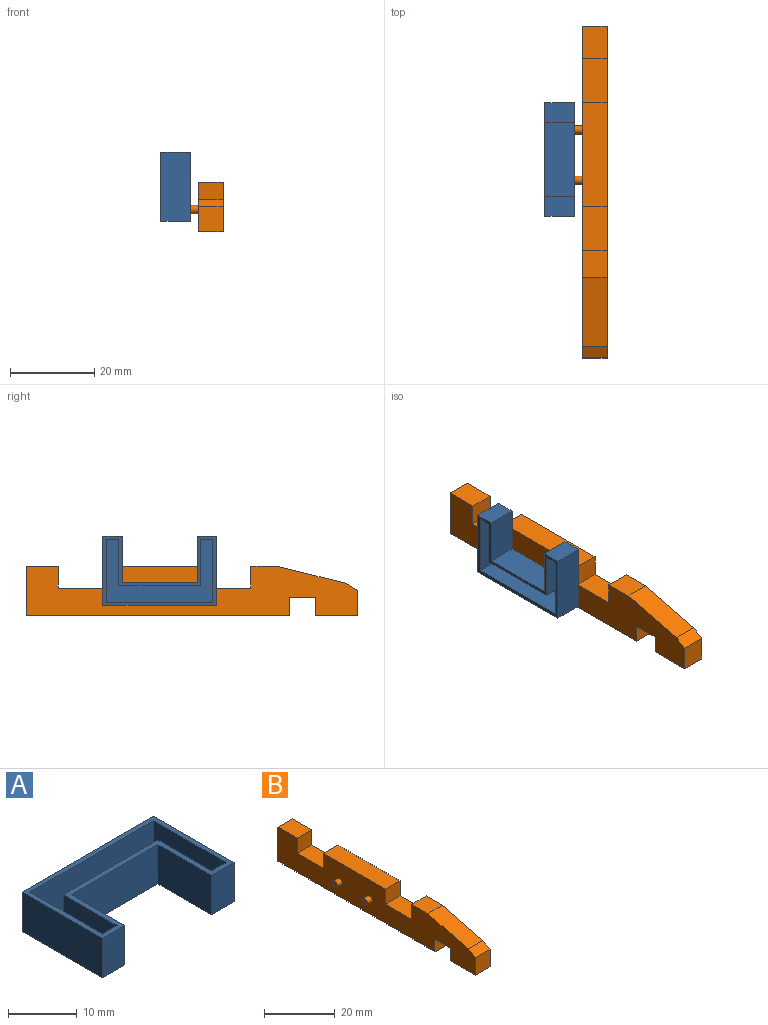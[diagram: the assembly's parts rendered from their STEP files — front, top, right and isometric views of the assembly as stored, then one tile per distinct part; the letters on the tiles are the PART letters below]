
ASSEMBLY  parts=2 mates=2
PART A: 19 faces, bbox 27x16.5x7 mm
  f0: plane 14.9x6.2mm, normal (1,0,0), area 92.4mm2, adj f1,f15,f16,f18
  f1: plane 25.4x6.2mm, normal (0,-1,0), area 157.5mm2, adj f0,f2,f16,f18
  f2: plane 14.9x6.2mm, normal (-1,0,0), area 92.4mm2, adj f1,f3,f16,f18
  f3: plane 6.2x3mm, normal (0,1,0), area 18.6mm2, adj f2,f4,f16,f18
  f4: plane 11x6.2mm, normal (1,0,0), area 68.2mm2, adj f3,f5,f16,f18
  f5: plane 19.4x6.2mm, normal (0,1,0), area 120.3mm2, adj f4,f6,f16,f18
  f6: plane 11x6.2mm, normal (-1,0,0), area 68.2mm2, adj f5,f15,f16,f18
  f7: plane 16.5x7mm, normal (-1,0,0), area 115.5mm2, adj f8,f14,f16,f17
  f8: plane 7x4.6mm, normal (0,-1,0), area 32.2mm2, adj f7,f9,f16,f17
  f9: plane 11x7mm, normal (1,0,0), area 77mm2, adj f8,f10,f16,f17
  f10: plane 17.8x7mm, normal (0,-1,0), area 124.6mm2, adj f9,f11,f16,f17
  f11: plane 11x7mm, normal (-1,0,0), area 77mm2, adj f10,f12,f16,f17
  f12: plane 7x4.6mm, normal (0,-1,0), area 32.2mm2, adj f11,f13,f16,f17
  f13: plane 16.5x7mm, normal (1,0,0), area 115.5mm2, adj f12,f14,f16,f17
  f14: plane 27x7mm, normal (0,1,0), area 189mm2, adj f7,f13,f16,f17
  f15: plane 6.2x3mm, normal (0,1,0), area 18.6mm2, adj f0,f6,f16,f18
  f16: plane 27x16.5mm, normal (0,0,1), area 84.6mm2, adj f0,f1,f2,f3,f4,f5,f6,f7
  f17: plane 27x16.5mm, normal (0,0,-1), area 249.7mm2, adj f7,f8,f9,f10,f11,f12,f13,f14
  f18: plane 25.4x14.9mm, normal (0,0,1), area 165.1mm2, adj f0,f1,f2,f3,f4,f5,f6,f15
PART B: 42 faces, bbox 7.8x79x11.8 mm
  f0: plane 5.1x5mm, normal (0,1,0), area 25.5mm2, adj f1,f17,f35,f37
  f1: plane 7.8x5mm, normal (0,0,1), area 39mm2, adj f0,f2,f35,f37
  f2: plane 5x4.3mm, normal (0,-1,0), area 21.5mm2, adj f1,f3,f35,f37
  f3: plane 8.4x5mm, normal (0,0,1), area 42mm2, adj f2,f4,f35,f37
  f4: plane 5x4.75mm, normal (0,1,0), area 23.7mm2, adj f3,f5,f35,f37
  f5: plane 5x2.31mm, normal (0,0.52,-0.85), area 13.5mm2, adj f4,f6,f35,f37
  f6: plane 16.09x5mm, normal (0,0.24,-0.97), area 82.9mm2, adj f5,f7,f35,f37
  f7: plane 5.5x5mm, normal (0,0,-1), area 27.5mm2, adj f6,f8,f35,f37
  f8: plane 5.2x5mm, normal (0,-1,0), area 26mm2, adj f7,f9,f35,f37
  f9: plane 12.1x5mm, normal (0,0,-1), area 60.5mm2, adj f8,f10,f35,f37
  f10: plane 5.2x5mm, normal (0,1,0), area 26mm2, adj f9,f11,f35,f37
  f11: plane 23.2x5mm, normal (0,0,-1), area 116mm2, adj f10,f12,f35,f37
  f12: plane 5.2x5mm, normal (0,-1,0), area 26mm2, adj f11,f13,f35,f37
  f13: plane 12.1x5mm, normal (0,0,-1), area 60.5mm2, adj f12,f14,f35,f37
  f14: plane 5.2x5mm, normal (0,1,0), area 26mm2, adj f13,f15,f35,f37
  f15: plane 6.1x5mm, normal (0,0,-1), area 30.5mm2, adj f14,f16,f35,f37
  f16: plane 11x5mm, normal (0,-1,0), area 55mm2, adj f15,f17,f35,f37
  f17: plane 62.8x5.8mm, normal (0,0,-1), area 58.2mm2, adj f0,f16,f18,f34,f35,f36,f37
  f18: plane 11.8x5.8mm, normal (0,1,0), area 68.4mm2, adj f17,f19,f35,f36
  f19: plane 7.7x5.8mm, normal (0,0,1), area 44.7mm2, adj f18,f20,f35,f36
  f20: plane 5.8x5.2mm, normal (0,-1,0), area 30.2mm2, adj f19,f21,f35,f36
  f21: plane 10.5x5.8mm, normal (0,0,1), area 60.9mm2, adj f20,f22,f35,f36
  f22: plane 5.8x5.2mm, normal (0,1,0), area 30.2mm2, adj f21,f23,f35,f36
  f23: plane 24.8x5.8mm, normal (0,0,1), area 143.8mm2, adj f22,f24,f35,f36
  f24: plane 5.8x5.2mm, normal (0,-1,0), area 30.2mm2, adj f23,f25,f35,f36
  f25: plane 10.5x5.8mm, normal (0,0,1), area 60.9mm2, adj f24,f26,f35,f36
  f26: plane 5.8x5.2mm, normal (0,1,0), area 30.2mm2, adj f25,f27,f35,f36
  f27: plane 6.4x5.8mm, normal (0,0,1), area 37.1mm2, adj f26,f28,f35,f36
  f28: plane 16.3x5.8mm, normal (0,-0.24,0.97), area 97.5mm2, adj f27,f29,f35,f36
  f29: plane 5.8x2.8mm, normal (0,-0.52,0.85), area 19mm2, adj f28,f30,f35,f36
  f30: plane 6x5.8mm, normal (0,-1,0), area 34.8mm2, adj f29,f31,f35,f36
  f31: plane 10x5.8mm, normal (0,0,-1), area 58mm2, adj f30,f32,f35,f36
  f32: plane 5.8x4.3mm, normal (0,1,0), area 24.9mm2, adj f31,f33,f35,f36
  f33: plane 6.2x5.8mm, normal (0,0,-1), area 36mm2, adj f32,f34,f35,f36
  f34: plane 5.8x4.3mm, normal (0,-1,0), area 24.9mm2, adj f17,f33,f35,f36
  f35: plane 79x11.8mm, normal (1,0,0), area 113.5mm2, adj f0,f1,f2,f3,f4,f5,f6,f7
  f36: plane 79x11.8mm, normal (-1,0,0), area 742.8mm2, adj f17,f18,f19,f20,f21,f22,f23,f24
  f37: plane 77.4x11mm, normal (1,0,0), area 635.5mm2, adj f0,f1,f2,f3,f4,f5,f6,f7
  f38: cylinder r=1mm len=2mm, axis (1,0,0), area 12.6mm2, adj f36,f39
  f39: plane 2x2mm, normal (-1,0,0), area 3.1mm2, adj f38
  f40: cylinder r=1mm len=2mm, axis (1,0,0), area 12.6mm2, adj f36,f41
  f41: plane 2x2mm, normal (-1,0,0), area 3.1mm2, adj f40
PLACE A rot(axis=(-0.58,-0.58,0.58),120deg) t=(-2,33.71,18.97)mm
PLACE B at identity
MATE revolute A.f17 <-> B.f40  axis (-1,0,0) through (-2,42.29,5.3)mm
MATE revolute A.f17 <-> B.f38  axis (-1,0,0) through (-2,54.29,5.3)mm
